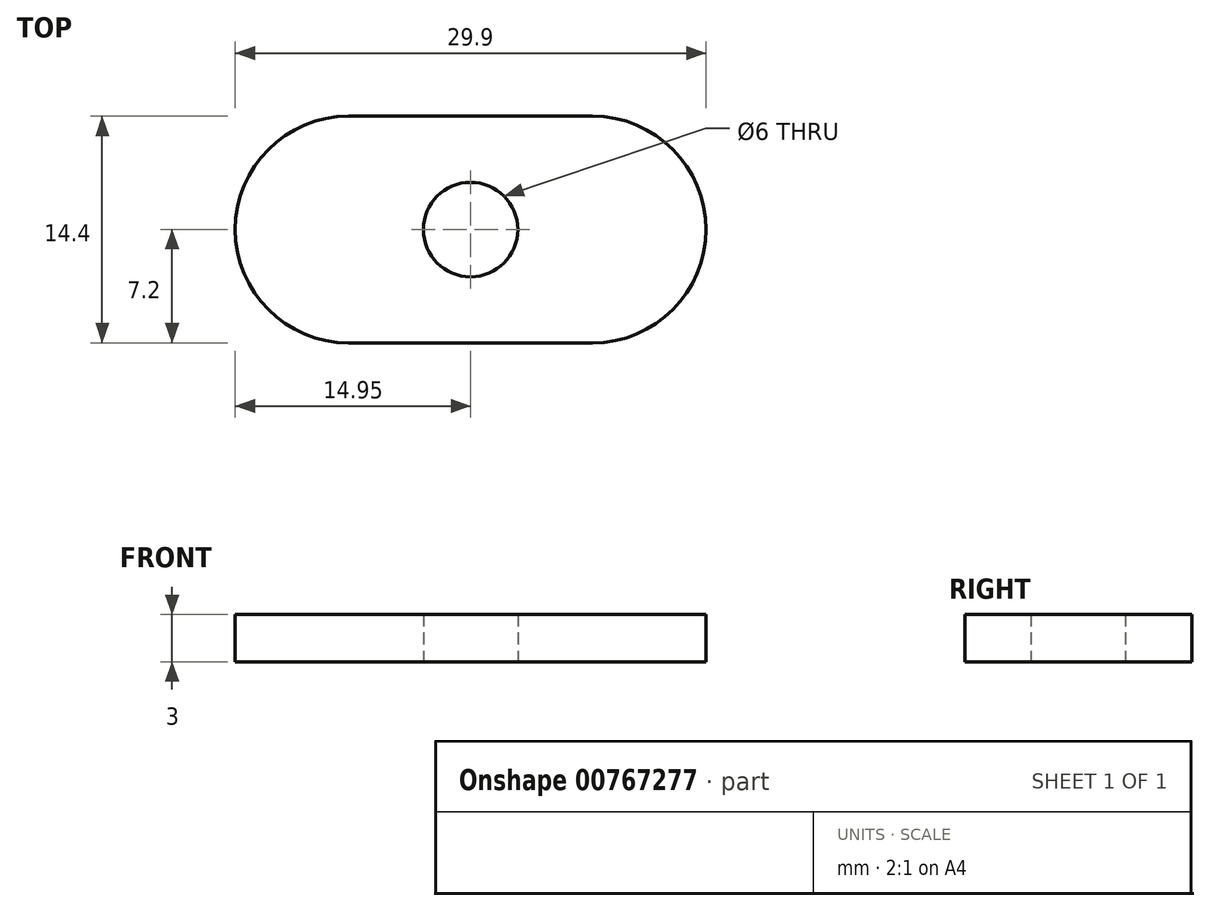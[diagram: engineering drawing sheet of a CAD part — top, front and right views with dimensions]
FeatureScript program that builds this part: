
annotation { "Feature Type Name" : "Feature", "Feature Type Description" : "" }
export const myFeature = defineFeature(function(context is Context, id is Id, definition is map)
    precondition{}
    {
        {
            var Q0;
            Q0=qCreatedBy(makeId("Top.planeOp"),FACE);
            var sketch = newSketch(context, id + "F0", { "sketchPlane" : qUnion([Q0])});
            skLineSegment(sketch, "E0.bottom", {"start": v(7.75, 7.2) * mm, "end": v(-7.75, 7.2) * mm});
            skLineSegment(sketch, "E0.top", {"start": v(7.75, -7.2) * mm, "end": v(-7.75, -7.2) * mm});
            skPoint(sketch, "E0.middle", {"position": v(0, 0) * mm});
            skCircle(sketch, "E1", {"center": v(0, 0) * mm, "radius": 3 * mm});
            skArc(sketch, "E2", {"start": v(-7.75, 7.2) * mm, "mid": v(-14.95, 0) * mm, "end": v(-7.75, -7.2) * mm});
            skArc(sketch, "E3", {"start": v(7.75, -7.2) * mm, "mid": v(14.95, 0) * mm, "end": v(7.75, 7.2) * mm});
            skSolve(sketch);
        }
        {
            var Q0;
            Q0=makeQuery(id+"F0.imprint","IMPRINT",FACE,{"disambiguationData":[TD([[makeQuery(id+"F0.imprint","IMPRINT",EDGE,{"derivedFrom":sQuery(id+"F0.wireOp",EDGE,"E0.bottom")}),1.0]])]});
            extrude(context, id + "F1", {"entities" : qUnion([Q0]), "depth" : 3 * mm, "offsetDistance" : 25 * mm});
        }
    });
